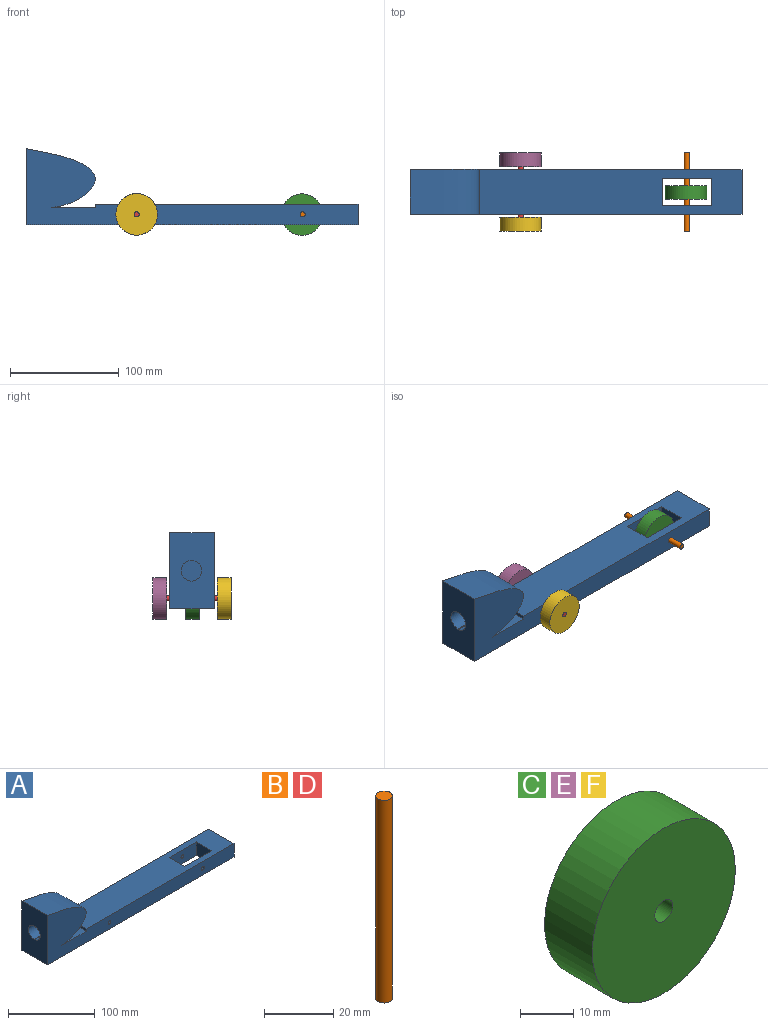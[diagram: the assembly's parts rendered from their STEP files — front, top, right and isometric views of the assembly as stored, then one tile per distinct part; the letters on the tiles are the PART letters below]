
ASSEMBLY  parts=6 mates=4
PART A: 21 faces, bbox 304.8x41.3x69.9 mm
  f0: cylinder r=2.38mm len=7.94mm, axis (0,1,0), area 118.8mm2, adj f2,f20
  f1: plane 69.85x41.28mm, normal (-1,0,0), area 2598mm2, adj f2,f3,f6,f13,f14,f15
  f2: plane 304.8x69.85mm, normal (0,1,0), area 8217mm2, adj f0,f1,f4,f5,f6,f7,f9,f10
  f3: plane 304.8x69.85mm, normal (0,-1,0), area 8217mm2, adj f1,f4,f5,f6,f7,f8,f9,f10
  f4: plane 41.28x0.58mm, normal (1,0,0), area 24mm2, adj f2,f3,f11,f13
  f5: plane 41.28x19.05mm, normal (1,0,0), area 786.3mm2, adj f2,f3,f6,f7
  f6: plane 304.8x41.28mm, normal (0,0,-1), area 11451.6mm2, adj f1,f2,f3,f5,f17,f18,f19,f20
  f7: plane 241.3x41.28mm, normal (0,0,1), area 8830.6mm2, adj f2,f3,f5,f12,f17,f18,f19,f20
  f8: cylinder r=2.38mm len=7.94mm, axis (0,1,0), area 118.8mm2, adj f3,f19
  f9: cylinder r=2.38mm len=41.28mm, axis (0,1,0), area 617.5mm2, adj f2,f3
  f10: plane 41.28x40.45mm, normal (0,0,1), area 1669.6mm2, adj f2,f3,f11,f12
  f11: extruded ~41.28x40.45mm, area 2120.4mm2, adj f2,f3,f4,f10
  f12: plane 41.28x3.19mm, normal (-1,0,0), area 131.6mm2, adj f2,f3,f7,f10
  f13: extruded ~63.5x41.28mm, area 2999mm2, adj f1,f2,f3,f4
  f14: plane 50.8x1mm, normal (0,0,1), area 50.6mm2, adj f1,f15,f16
  f15: cylinder r=9.53mm len=50.8mm, axis (-1,0,0), area 2989.6mm2, adj f1,f14,f16
  f16: plane 19.05x19.04mm, normal (-1,0,0), area 285mm2, adj f14,f15
  f17: plane 25.4x19.05mm, normal (1,0,0), area 483.9mm2, adj f6,f7,f19,f20
  f18: plane 25.4x19.05mm, normal (-1,0,0), area 483.9mm2, adj f6,f7,f19,f20
  f19: plane 44.45x19.05mm, normal (0,1,0), area 829mm2, adj f6,f7,f8,f17,f18
  f20: plane 44.45x19.05mm, normal (0,-1,0), area 829mm2, adj f0,f6,f7,f17,f18
PART B: 3 faces, bbox 4.8x4.8x71.8 mm
  f0: cylinder r=2.38mm len=71.76mm, axis (0,0,-1), area 1073mm2, adj f1,f2
  f1: plane 4.76x4.76mm, normal (0,0,1), area 17.8mm2, adj f0
  f2: plane 4.76x4.76mm, normal (0,0,-1), area 17.8mm2, adj f0
PART C: 4 faces, bbox 38.1x12.7x38.1 mm
  f0: cylinder r=19.05mm len=38.1mm, axis (0,1,0), area 1520.1mm2, adj f1,f2
  f1: plane 38.1x38.1mm, normal (0,-1,0), area 1122.3mm2, adj f0,f3
  f2: plane 38.1x38.1mm, normal (0,1,0), area 1122.3mm2, adj f0,f3
  f3: cylinder r=2.38mm len=12.7mm, axis (0,-1,0), area 190mm2, adj f1,f2
PART D: same geometry as B
PART E: same geometry as C
PART F: same geometry as C
PLACE A t=(-64.19,0.62,12.63)mm
PLACE B rot(axis=(-1,0,0),90deg) t=(189.81,-14.62,22.16)mm
PLACE C t=(189.25,27.11,21.97)mm
PLACE D rot(axis=(-1,0,0),90deg) t=(37.41,-14.62,22.16)mm
PLACE E rot(axis=(0,1,0),90deg) t=(37.41,57.13,22.16)mm
PLACE F t=(37.41,-1.92,22.16)mm
MATE revolute E.f0 <-> D.f0  axis (0,1,0) through (37.41,57.13,22.16)mm
MATE revolute F.f0 <-> D.f0  axis (0,-1,0) through (37.41,-14.62,22.16)mm
MATE fastened B.f0 <-> A.f0  axis (0,-1,0) through (189.81,-14.62,22.16)mm
MATE fastened A.f9 <-> D.f0  axis (0,-1,0) through (37.41,0.62,22.16)mm
